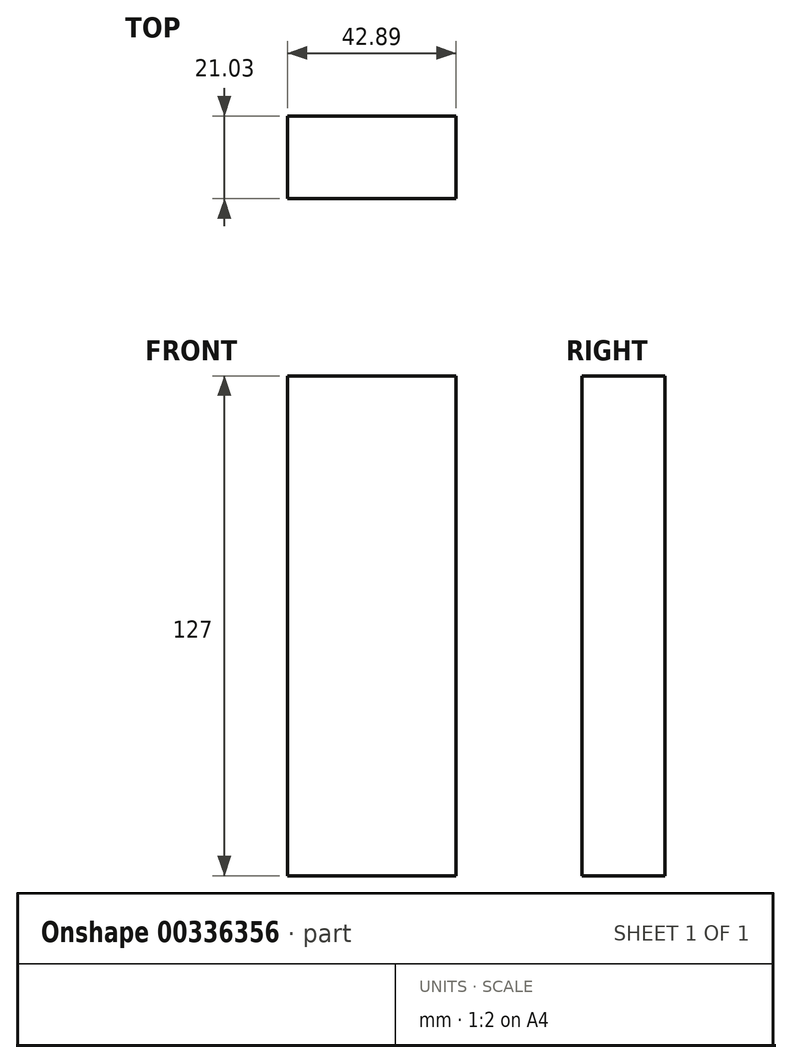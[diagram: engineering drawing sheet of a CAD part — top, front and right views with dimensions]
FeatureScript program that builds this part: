
annotation { "Feature Type Name" : "Feature", "Feature Type Description" : "" }
export const myFeature = defineFeature(function(context is Context, id is Id, definition is map)
    precondition{}
    {
        {
            var Q0;
            Q0=qCreatedBy(makeId("Top.planeOp"),FACE);
            var sketch = newSketch(context, id + "F0", { "sketchPlane" : qUnion([Q0])});
            skLineSegment(sketch, "E0.bottom", {"start": v(-44.73, 60.25) * mm, "end": v(-33.65, 60.25) * mm});
            skLineSegment(sketch, "E0.top", {"start": v(-44.73, 73.43) * mm, "end": v(-33.65, 73.43) * mm});
            skLineSegment(sketch, "E0.left", {"start": v(-44.73, 60.25) * mm, "end": v(-44.73, 73.43) * mm});
            skLineSegment(sketch, "E0.right", {"start": v(-33.65, 60.25) * mm, "end": v(-33.65, 73.43) * mm});
            skLineSegment(sketch, "E1.bottom", {"start": v(27.92, 43.32) * mm, "end": v(48.1, 43.32) * mm});
            skLineSegment(sketch, "E1.top", {"start": v(27.92, 74.23) * mm, "end": v(48.1, 74.23) * mm});
            skLineSegment(sketch, "E1.left", {"start": v(27.92, 43.32) * mm, "end": v(27.92, 74.23) * mm});
            skLineSegment(sketch, "E1.right", {"start": v(48.1, 43.32) * mm, "end": v(48.1, 74.23) * mm});
            skPoint(sketch, "E2.oppositeSnap0", {"position": v(48.1, 58.78) * mm});
            skLineSegment(sketch, "E2.bottom", {"start": v(48.1, 82.35) * mm, "end": v(63.5, 82.35) * mm});
            skLineSegment(sketch, "E2.top", {"start": v(48.1, 58.78) * mm, "end": v(63.5, 58.78) * mm});
            skLineSegment(sketch, "E2.left", {"start": v(48.1, 82.35) * mm, "end": v(48.1, 58.78) * mm});
            skLineSegment(sketch, "E2.right", {"start": v(63.5, 82.35) * mm, "end": v(63.5, 58.78) * mm});
            skLineSegment(sketch, "E3.bottom", {"start": v(61.82, -29.52) * mm, "end": v(18.93, -29.52) * mm});
            skLineSegment(sketch, "E3.top", {"start": v(61.82, -50.55) * mm, "end": v(18.93, -50.55) * mm});
            skLineSegment(sketch, "E3.left", {"start": v(61.82, -29.52) * mm, "end": v(61.82, -50.55) * mm});
            skLineSegment(sketch, "E3.right", {"start": v(18.93, -29.52) * mm, "end": v(18.93, -50.55) * mm});
            skPoint(sketch, "E3.middle", {"position": v(40.37, -40.03) * mm});
            skSolve(sketch);
        }
        {
            var Q0;
            Q0=makeQuery(id+"F0.imprint","IMPRINT",FACE,{"disambiguationData":[TD([[makeQuery(id+"F0.imprint","IMPRINT",EDGE,{"derivedFrom":sQuery(id+"F0.wireOp",EDGE,"E3.bottom")}),1.0]])]});
            extrude(context, id + "F1", {"entities" : qUnion([Q0]), "depth" : 127 * mm});
        }
    });
